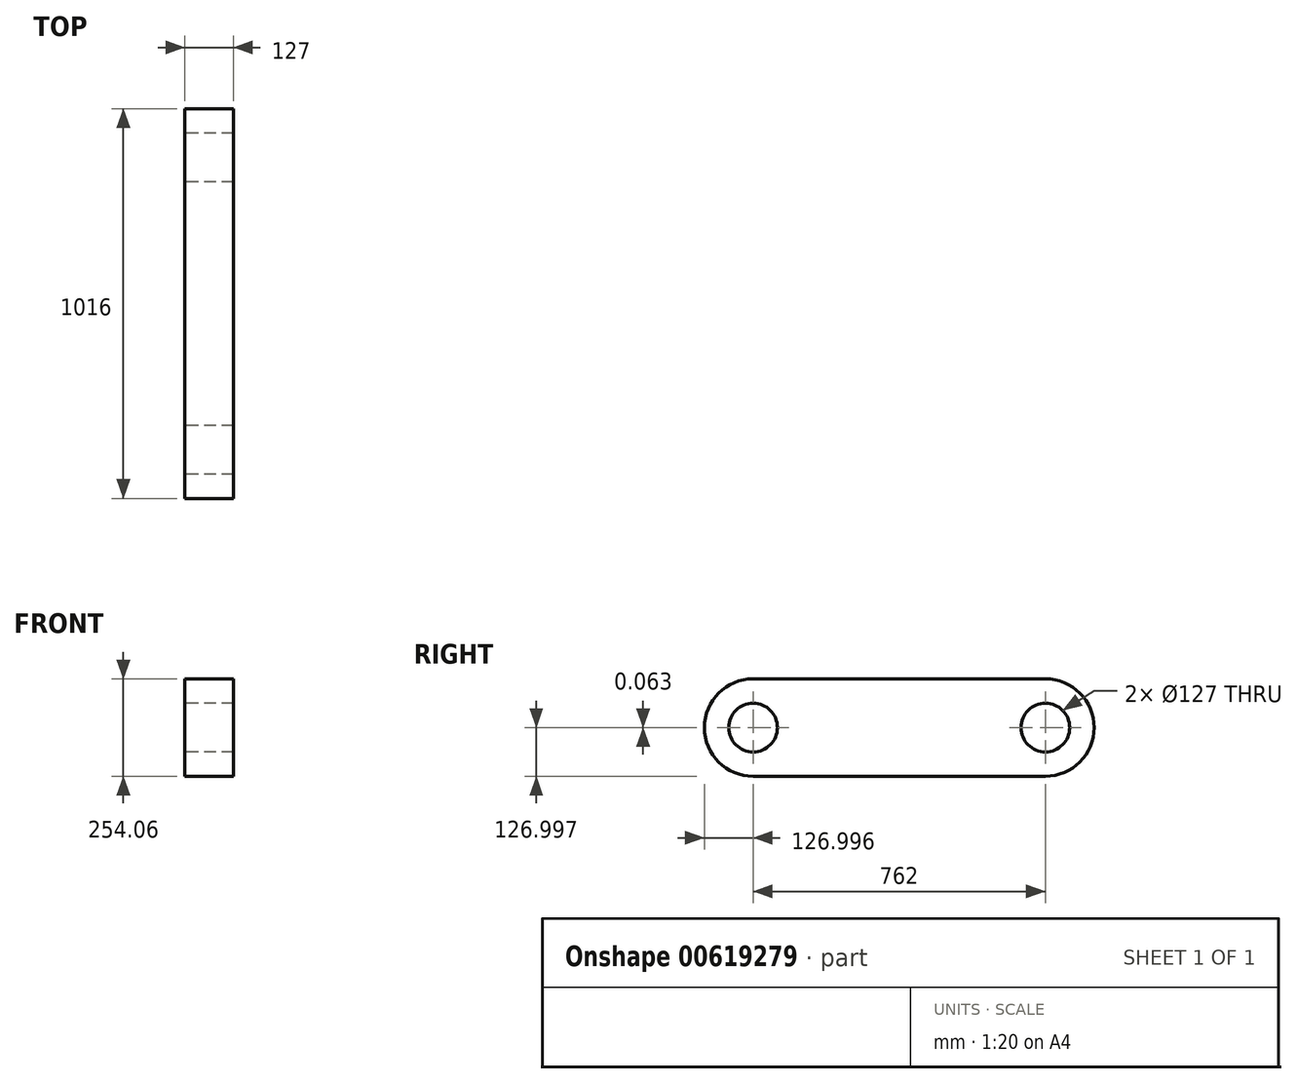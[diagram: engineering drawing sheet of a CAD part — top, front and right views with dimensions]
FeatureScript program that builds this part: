
annotation { "Feature Type Name" : "Feature", "Feature Type Description" : "" }
export const myFeature = defineFeature(function(context is Context, id is Id, definition is map)
    precondition{}
    {
        {
            var Q0;
            Q0=qCreatedBy(makeId("Right.planeOp"),FACE);
            var sketch = newSketch(context, id + "F0", { "sketchPlane" : qUnion([Q0])});
            skArc(sketch, "E0", {"start": v(-34.95, 126.94) * mm, "mid": v(-161.94, -0.07) * mm, "end": v(-34.93, -127.06) * mm});
            skArc(sketch, "E1", {"start": v(727.07, -127) * mm, "mid": v(854.06, 0.01) * mm, "end": v(727.05, 127) * mm});
            skLineSegment(sketch, "E2", {"start": v(-34.95, 126.94) * mm, "end": v(727.05, 127) * mm});
            skLineSegment(sketch, "E3", {"start": v(-34.93, -127.06) * mm, "end": v(727.07, -127) * mm});
            skCircle(sketch, "E4", {"center": v(-34.94, -0.06) * mm, "radius": 63.5 * mm});
            skCircle(sketch, "E5", {"center": v(727.06, 0) * mm, "radius": 63.5 * mm});
            skSolve(sketch);
        }
        {
            var Q0;
            Q0=makeQuery(id+"F0.imprint","IMPRINT",FACE,{"disambiguationData":[TD([[makeQuery(id+"F0.imprint","IMPRINT",EDGE,{"derivedFrom":sQuery(id+"F0.wireOp",EDGE,"E0")}),1.0]])]});
            extrude(context, id + "F1", {"entities" : qUnion([Q0]), "depth" : 127 * mm, "offsetDistance" : 25.4 * mm});
        }
    });
